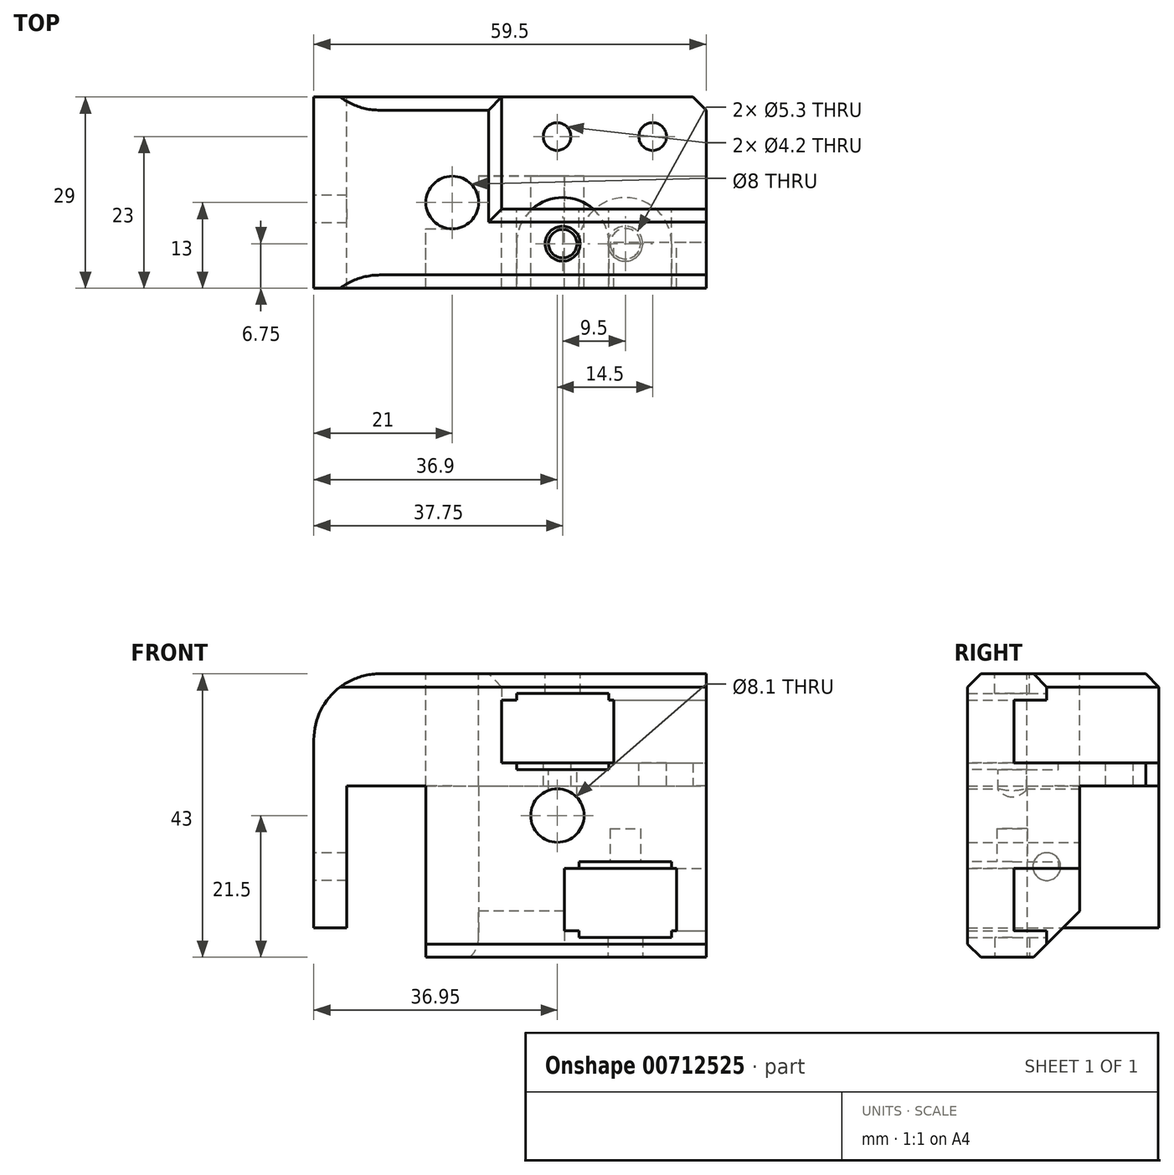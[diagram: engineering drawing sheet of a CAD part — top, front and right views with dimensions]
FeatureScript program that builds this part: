
annotation { "Feature Type Name" : "Feature", "Feature Type Description" : "" }
export const myFeature = defineFeature(function(context is Context, id is Id, definition is map)
    precondition{}
    {
        {
            var Q0;
            Q0=qCreatedBy(makeId("Front.planeOp"),FACE);
            var sketch = newSketch(context, id + "F0", { "sketchPlane" : qUnion([Q0])});
            skLineSegment(sketch, "E0", {"start": v(0, 0) * mm, "end": v(0, 28.5) * mm});
            skLineSegment(sketch, "E1", {"start": v(10, 38.5) * mm, "end": v(59.5, 38.5) * mm});
            skLineSegment(sketch, "E2", {"start": v(59.5, 38.5) * mm, "end": v(59.5, -4.5) * mm});
            skLineSegment(sketch, "E3", {"start": v(59.5, -4.5) * mm, "end": v(17, -4.5) * mm});
            skLineSegment(sketch, "E4", {"start": v(17, -4.5) * mm, "end": v(17, 21.5) * mm});
            skLineSegment(sketch, "E5", {"start": v(17, 21.5) * mm, "end": v(5, 21.5) * mm});
            skLineSegment(sketch, "E6", {"start": v(5, 21.5) * mm, "end": v(5, 0) * mm});
            skLineSegment(sketch, "E7", {"start": v(5, 0) * mm, "end": v(0, 0) * mm});
            skPoint(sketch, "E8.visualSharp", {"position": v(0, 38.5) * mm});
            skArc(sketch, "E8.filletArc", {"start": v(10, 38.5) * mm, "mid": v(2.93, 35.57) * mm, "end": v(0, 28.5) * mm});
            skCircle(sketch, "E9", {"center": v(36.95, 17) * mm, "radius": 4.05 * mm});
            skLineSegment(sketch, "E10.bottom", {"start": v(28.5, 34.5) * mm, "end": v(45.5, 34.5) * mm});
            skLineSegment(sketch, "E10.top", {"start": v(28.5, 25) * mm, "end": v(45.5, 25) * mm});
            skLineSegment(sketch, "E10.left", {"start": v(28.5, 34.5) * mm, "end": v(28.5, 25) * mm});
            skLineSegment(sketch, "E10.right", {"start": v(45.5, 34.5) * mm, "end": v(45.5, 25) * mm});
            skLineSegment(sketch, "E11.bottom", {"start": v(38, 9) * mm, "end": v(55, 9) * mm});
            skLineSegment(sketch, "E11.top", {"start": v(38, -0.5) * mm, "end": v(55, -0.5) * mm});
            skLineSegment(sketch, "E11.left", {"start": v(38, 9) * mm, "end": v(38, -0.5) * mm});
            skLineSegment(sketch, "E11.right", {"start": v(55, 9) * mm, "end": v(55, -0.5) * mm});
            skLineSegment(sketch, "E12.bottom", {"start": v(30.75, 34.5) * mm, "end": v(44.75, 34.5) * mm});
            skLineSegment(sketch, "E12.top", {"start": v(30.75, 35.5) * mm, "end": v(44.75, 35.5) * mm});
            skLineSegment(sketch, "E12.left", {"start": v(30.75, 34.5) * mm, "end": v(30.75, 35.5) * mm});
            skLineSegment(sketch, "E12.right", {"start": v(44.75, 34.5) * mm, "end": v(44.75, 35.5) * mm});
            skLineSegment(sketch, "E13.bottom", {"start": v(40.25, -0.5) * mm, "end": v(54.25, -0.5) * mm});
            skLineSegment(sketch, "E13.top", {"start": v(40.25, -1.5) * mm, "end": v(54.25, -1.5) * mm});
            skLineSegment(sketch, "E13.left", {"start": v(40.25, -0.5) * mm, "end": v(40.25, -1.5) * mm});
            skLineSegment(sketch, "E13.right", {"start": v(54.25, -0.5) * mm, "end": v(54.25, -1.5) * mm});
            skSolve(sketch);
        }
        {
            var Q0;
            Q0=makeQuery(id+"F0.imprint","IMPRINT",FACE,{"disambiguationData":[TD([[makeQuery(id+"F0.imprint","IMPRINT",EDGE,{"derivedFrom":sQuery(id+"F0.wireOp",EDGE,"E0")}),-1.0]])]});
            extrude(context, id + "F1", {"entities" : qUnion([Q0]), "depth" : 7 * mm, "offsetDistance" : 25 * mm});
        }
        {
            var Q0;
            Q0=makeQuery(id+"F1.opExtrude","CAP_EDGE",EDGE,{"disambiguationData":[OSD([sQuery(id+"F0.wireOp",EDGE,"E1")])],"isStart":false});
            var Q1;
            Q1=makeQuery(id+"F1.opExtrude","CAP_EDGE",EDGE,{"disambiguationData":[OSD([sQuery(id+"F0.wireOp",EDGE,"E3")])],"isStart":false});
            chamfer(context, id + "F2", {"entities" : qUnion([Q0, Q1]), "width" : 2 * mm});
        }
        {
            var Q0;
            Q0=makeQuery(id+"F1.opExtrude","CAP_FACE",FACE,{"disambiguationData":[OSD([sQuery(id+"F0.wireOp",EDGE,"E0"),sQuery(id+"F0.wireOp",EDGE,"E1"),sQuery(id+"F0.wireOp",EDGE,"E2"),sQuery(id+"F0.wireOp",EDGE,"E3"),sQuery(id+"F0.wireOp",EDGE,"E4"),sQuery(id+"F0.wireOp",EDGE,"E5"),sQuery(id+"F0.wireOp",EDGE,"E6"),sQuery(id+"F0.wireOp",EDGE,"E7"),sQuery(id+"F0.wireOp",EDGE,"E8.filletArc"),sQuery(id+"F0.wireOp",EDGE,"E9"),sQuery(id+"F0.wireOp",EDGE,"E10.bottom"),sQuery(id+"F0.wireOp",EDGE,"E10.top"),sQuery(id+"F0.wireOp",EDGE,"E10.left"),sQuery(id+"F0.wireOp",EDGE,"E10.right"),sQuery(id+"F0.wireOp",EDGE,"E11.bottom"),sQuery(id+"F0.wireOp",EDGE,"E11.top"),sQuery(id+"F0.wireOp",EDGE,"E11.left"),sQuery(id+"F0.wireOp",EDGE,"E11.right"),sQuery(id+"F0.wireOp",EDGE,"E12.top"),sQuery(id+"F0.wireOp",EDGE,"E12.left"),sQuery(id+"F0.wireOp",EDGE,"E12.right"),sQuery(id+"F0.wireOp",EDGE,"E13.top"),sQuery(id+"F0.wireOp",EDGE,"E13.left"),sQuery(id+"F0.wireOp",EDGE,"E13.right")])],"isStart":true});
            var sketch = newSketch(context, id + "F3", { "sketchPlane" : qUnion([Q0])});
            skLineSegment(sketch, "E14.bottom", {"start": v(-17, 21.5) * mm, "end": v(-59.5, 21.5) * mm});
            skLineSegment(sketch, "E14.top", {"start": v(-17, -4.5) * mm, "end": v(-59.5, -4.5) * mm});
            skLineSegment(sketch, "E14.left", {"start": v(-17, 21.5) * mm, "end": v(-17, -4.5) * mm});
            skLineSegment(sketch, "E14.right", {"start": v(-59.5, 21.5) * mm, "end": v(-59.5, -4.5) * mm});
            skLineSegment(sketch, "E15.bottom", {"start": v(-59.5, 38.5) * mm, "end": v(-28.5, 38.5) * mm});
            skLineSegment(sketch, "E15.top", {"start": v(-59.5, 25) * mm, "end": v(-28.5, 25) * mm});
            skLineSegment(sketch, "E15.left", {"start": v(-59.5, 38.5) * mm, "end": v(-59.5, 25) * mm});
            skLineSegment(sketch, "E15.right", {"start": v(-28.5, 38.5) * mm, "end": v(-28.5, 25) * mm});
            skSolve(sketch);
        }
        {
            var Q0;
            {var subQ0=sQuery(id+"F3.wireOp",EDGE,"E14.bottom");Q0=makeQuery(id+"F3.imprint","IMPRINT",FACE,{"disambiguationData":[TD([[makeQuery(id+"F3.imprint","IMPRINT",EDGE,{"derivedFrom":subQ0}),-1.0]])]});}
            extrude(context, id + "F4", {"entities" : qUnion([Q0]), "operationType" : NewBodyOperationType.ADD, "depth" : 22 * mm, "offsetDistance" : 25 * mm});
        }
        {
            var Q0;
            {var subQ0=sQuery(id+"F0.wireOp",EDGE,"E12.top");var subQ1=sQuery(id+"F0.wireOp",EDGE,"E10.right");var subQ2=sQuery(id+"F0.wireOp",EDGE,"E10.top");var subQ3=sQuery(id+"F0.wireOp",EDGE,"E1");var subQ4=sQuery(id+"F0.wireOp",EDGE,"E12.right");var subQ5=sQuery(id+"F0.wireOp",EDGE,"E10.bottom");var subQ7=sQuery(id+"F0.wireOp",EDGE,"E10.left");var subQ8=sQuery(id+"F0.wireOp",EDGE,"E2");var subQ9=sQuery(id+"F0.wireOp",EDGE,"E12.left");Q0=makeQuery(id+"F4.boolean.opBoolean","SPLIT",FACE,{"disambiguationData":[TD([makeQuery(id+"F1.opExtrude","SWEPT_FACE",FACE,{"disambiguationData":[OSD([subQ3])]})])],"derivedFrom":makeQuery(id+"F1.opExtrude","CAP_FACE",FACE,{"disambiguationData":[OSD([sQuery(id+"F0.wireOp",EDGE,"E0"),subQ3,subQ8,sQuery(id+"F0.wireOp",EDGE,"E3"),sQuery(id+"F0.wireOp",EDGE,"E4"),sQuery(id+"F0.wireOp",EDGE,"E5"),sQuery(id+"F0.wireOp",EDGE,"E6"),sQuery(id+"F0.wireOp",EDGE,"E7"),sQuery(id+"F0.wireOp",EDGE,"E8.filletArc"),sQuery(id+"F0.wireOp",EDGE,"E9"),subQ5,subQ2,subQ7,subQ1,sQuery(id+"F0.wireOp",EDGE,"E11.bottom"),sQuery(id+"F0.wireOp",EDGE,"E11.top"),sQuery(id+"F0.wireOp",EDGE,"E11.left"),sQuery(id+"F0.wireOp",EDGE,"E11.right"),subQ0,subQ9,subQ4,sQuery(id+"F0.wireOp",EDGE,"E13.top"),sQuery(id+"F0.wireOp",EDGE,"E13.left"),sQuery(id+"F0.wireOp",EDGE,"E13.right")])],"isStart":true})});}
            var sketch = newSketch(context, id + "F5", { "sketchPlane" : qUnion([Q0])});
            skLineSegment(sketch, "E16.bottom", {"start": v(-28.5, 34.5) * mm, "end": v(-59.5, 34.5) * mm});
            skLineSegment(sketch, "E16.top", {"start": v(-28.5, 38.5) * mm, "end": v(-59.5, 38.5) * mm});
            skLineSegment(sketch, "E16.left", {"start": v(-28.5, 34.5) * mm, "end": v(-28.5, 38.5) * mm});
            skLineSegment(sketch, "E16.right", {"start": v(-59.5, 34.5) * mm, "end": v(-59.5, 38.5) * mm});
            skSolve(sketch);
        }
        {
            var Q0;
            Q0=makeQuery(id+"F5.imprint","IMPRINT",FACE,{"disambiguationData":[TD([[makeQuery(id+"F5.imprint","IMPRINT",EDGE,{"derivedFrom":sQuery(id+"F5.wireOp",EDGE,"E16.top")}),1.0]])]});
            extrude(context, id + "F6", {"entities" : qUnion([Q0]), "operationType" : NewBodyOperationType.ADD, "depth" : 5 * mm, "offsetDistance" : 25 * mm});
        }
        {
            var Q0;
            {var subQ0=sQuery(id+"F0.wireOp",EDGE,"E11.right");var subQ1=sQuery(id+"F0.wireOp",EDGE,"E11.left");var subQ2=sQuery(id+"F0.wireOp",EDGE,"E2");var subQ3=sQuery(id+"F0.wireOp",EDGE,"E11.top");var subQ4=sQuery(id+"F0.wireOp",EDGE,"E13.right");var subQ6=sQuery(id+"F0.wireOp",EDGE,"E9");var subQ7=sQuery(id+"F0.wireOp",EDGE,"E3");var subQ8=sQuery(id+"F0.wireOp",EDGE,"E11.bottom");var subQ9=sQuery(id+"F0.wireOp",EDGE,"E4");var subQ10=sQuery(id+"F0.wireOp",EDGE,"E13.left");var subQ11=sQuery(id+"F0.wireOp",EDGE,"E5");var subQ12=sQuery(id+"F0.wireOp",EDGE,"E13.top");Q0=makeQuery(id+"F4.boolean.opBoolean","SPLIT",FACE,{"disambiguationData":[TD([makeQuery(id+"F1.opExtrude","SWEPT_FACE",FACE,{"disambiguationData":[OSD([subQ7])]})])],"derivedFrom":makeQuery(id+"F1.opExtrude","CAP_FACE",FACE,{"disambiguationData":[OSD([sQuery(id+"F0.wireOp",EDGE,"E0"),sQuery(id+"F0.wireOp",EDGE,"E1"),subQ2,subQ7,subQ9,subQ11,sQuery(id+"F0.wireOp",EDGE,"E6"),sQuery(id+"F0.wireOp",EDGE,"E7"),sQuery(id+"F0.wireOp",EDGE,"E8.filletArc"),subQ6,sQuery(id+"F0.wireOp",EDGE,"E10.bottom"),sQuery(id+"F0.wireOp",EDGE,"E10.top"),sQuery(id+"F0.wireOp",EDGE,"E10.left"),sQuery(id+"F0.wireOp",EDGE,"E10.right"),subQ8,subQ3,subQ1,subQ0,sQuery(id+"F0.wireOp",EDGE,"E12.top"),sQuery(id+"F0.wireOp",EDGE,"E12.left"),sQuery(id+"F0.wireOp",EDGE,"E12.right"),subQ12,subQ10,subQ4])],"isStart":true})});}
            var sketch = newSketch(context, id + "F7", { "sketchPlane" : qUnion([Q0])});
            skLineSegment(sketch, "E17.bottom", {"start": v(-38, -0.5) * mm, "end": v(-59.5, -0.5) * mm});
            skLineSegment(sketch, "E17.top", {"start": v(-38, 9) * mm, "end": v(-59.5, 9) * mm});
            skLineSegment(sketch, "E17.left", {"start": v(-38, -0.5) * mm, "end": v(-38, 9) * mm});
            skLineSegment(sketch, "E17.right", {"start": v(-59.5, -0.5) * mm, "end": v(-59.5, 9) * mm});
            skSolve(sketch);
        }
        {
            var Q0;
            {var subQ5=sQuery(id+"F7.wireOp",EDGE,"E17.left");Q0=makeQuery(id+"F7.imprint","IMPRINT",FACE,{"disambiguationData":[TD([[makeQuery(id+"F7.imprint","IMPRINT",EDGE,{"derivedFrom":subQ5}),1.0]])]});}
            extrude(context, id + "F8", {"entities" : qUnion([Q0]), "operationType" : NewBodyOperationType.ADD, "depth" : 2 * mm, "offsetDistance" : 25 * mm});
        }
        {
            var Q0;
            Q0=makeQuery(id+"F8.opExtrude","CAP_FACE",FACE,{"disambiguationData":[OSD([sQuery(id+"F0.wireOp",EDGE,"E2"),sQuery(id+"F0.wireOp",EDGE,"E3"),sQuery(id+"F0.wireOp",EDGE,"E4"),sQuery(id+"F0.wireOp",EDGE,"E5"),sQuery(id+"F0.wireOp",EDGE,"E9"),sQuery(id+"F0.wireOp",EDGE,"E13.top"),sQuery(id+"F0.wireOp",EDGE,"E13.left"),sQuery(id+"F0.wireOp",EDGE,"E13.right"),sQuery(id+"F3.wireOp",EDGE,"E14.bottom"),sQuery(id+"F7.wireOp",EDGE,"E17.bottom"),sQuery(id+"F7.wireOp",EDGE,"E17.top"),sQuery(id+"F7.wireOp",EDGE,"E17.left")])],"isStart":false});
            var sketch = newSketch(context, id + "F9", { "sketchPlane" : qUnion([Q0])});
            skLineSegment(sketch, "E18.bottom", {"start": v(-17, 21.5) * mm, "end": v(-21, 21.5) * mm});
            skLineSegment(sketch, "E18.top", {"start": v(-17, -4.5) * mm, "end": v(-21, -4.5) * mm});
            skLineSegment(sketch, "E18.left", {"start": v(-17, 21.5) * mm, "end": v(-17, -4.5) * mm});
            skLineSegment(sketch, "E18.right", {"start": v(-21, 21.5) * mm, "end": v(-21, -4.5) * mm});
            skSolve(sketch);
        }
        {
            var Q0;
            {var subQ15=sQuery(id+"F9.wireOp",EDGE,"E18.right");Q0=makeQuery(id+"F9.imprint","IMPRINT",FACE,{"disambiguationData":[TD([[makeQuery(id+"F9.imprint","IMPRINT",EDGE,{"derivedFrom":subQ15}),-1.0]])]});}
            extrude(context, id + "F10", {"entities" : qUnion([Q0]), "operationType" : NewBodyOperationType.ADD, "depth" : 3 * mm, "offsetDistance" : 25 * mm});
        }
        {
            var Q0;
            Q0=makeQuery(id+"F10.opExtrude","CAP_FACE",FACE,{"disambiguationData":[OSD([sQuery(id+"F0.wireOp",EDGE,"E2"),sQuery(id+"F0.wireOp",EDGE,"E3"),sQuery(id+"F0.wireOp",EDGE,"E5"),sQuery(id+"F0.wireOp",EDGE,"E9"),sQuery(id+"F0.wireOp",EDGE,"E13.top"),sQuery(id+"F0.wireOp",EDGE,"E13.left"),sQuery(id+"F0.wireOp",EDGE,"E13.right"),sQuery(id+"F3.wireOp",EDGE,"E14.bottom"),sQuery(id+"F7.wireOp",EDGE,"E17.bottom"),sQuery(id+"F7.wireOp",EDGE,"E17.top"),sQuery(id+"F7.wireOp",EDGE,"E17.left"),sQuery(id+"F9.wireOp",EDGE,"E18.right")])],"isStart":false});
            var sketch = newSketch(context, id + "F11", { "sketchPlane" : qUnion([Q0])});
            skLineSegment(sketch, "E19.bottom", {"start": v(-38, -0.5) * mm, "end": v(-59.5, -0.5) * mm});
            skLineSegment(sketch, "E19.top", {"start": v(-38, -4.5) * mm, "end": v(-59.5, -4.5) * mm});
            skLineSegment(sketch, "E19.left", {"start": v(-38, -0.5) * mm, "end": v(-38, -4.5) * mm});
            skLineSegment(sketch, "E19.right", {"start": v(-59.5, -0.5) * mm, "end": v(-59.5, -4.5) * mm});
            skSolve(sketch);
        }
        {
            var Q0;
            {var subQ2=sQuery(id+"F11.wireOp",EDGE,"E19.left");Q0=makeQuery(id+"F11.imprint","IMPRINT",FACE,{"disambiguationData":[TD([[makeQuery(id+"F11.imprint","IMPRINT",EDGE,{"derivedFrom":subQ2}),1.0]])]});}
            extrude(context, id + "F12", {"entities" : qUnion([Q0]), "operationType" : NewBodyOperationType.ADD, "depth" : 5 * mm, "offsetDistance" : 25 * mm});
        }
        {
            var Q0;
            Q0=makeQuery(id+"F12.opExtrude","CAP_EDGE",EDGE,{"disambiguationData":[OSD([sQuery(id+"F0.wireOp",EDGE,"E3")])],"isStart":false});
            chamfer(context, id + "F13", {"entities" : qUnion([Q0]), "width" : 7 * mm, "tangentPropagation" : true});
        }
        {
            var Q0;
            Q0=makeQuery(id+"F6.opExtrude","CAP_EDGE",EDGE,{"disambiguationData":[OSD([sQuery(id+"F5.wireOp",EDGE,"E16.top")])],"isStart":false});
            var Q1;
            Q1=makeQuery(id+"F4.opExtrude","CAP_EDGE",EDGE,{"disambiguationData":[OSD([sQuery(id+"F0.wireOp",EDGE,"E2")])],"isStart":false});
            chamfer(context, id + "F14", {"entities" : qUnion([Q0, Q1]), "width" : 2 * mm, "tangentPropagation" : true});
        }
        {
            var Q0;
            Q0=qCreatedBy(makeId("Top.planeOp"),FACE);
            var sketch = newSketch(context, id + "F15", { "sketchPlane" : qUnion([Q0])});
            skCircle(sketch, "E20", {"center": v(21, 6) * mm, "radius": 4 * mm});
            skSolve(sketch);
        }
        {
            var Q0;
            {var subQ0=sQuery(id+"F9.wireOp",EDGE,"E18.right");Q0=makeQuery(id+"F12.boolean.opBoolean","MERGE",FACE,{"derivedFrom":[makeQuery(id+"F10.opExtrude","SWEPT_FACE",FACE,{"disambiguationData":[OSD([subQ0])]}),makeQuery(id+"F12.opExtrude","SWEPT_FACE",FACE,{"disambiguationData":[OSD([subQ0])]})]});}
            var sketch = newSketch(context, id + "F16", { "sketchPlane" : qUnion([Q0])});
            skLineSegment(sketch, "E21.bottom", {"start": v(-10, 21.5) * mm, "end": v(-6, 21.5) * mm});
            skLineSegment(sketch, "E21.top", {"start": v(-10, -13.36) * mm, "end": v(-6, -13.36) * mm});
            skLineSegment(sketch, "E21.left", {"start": v(-10, 21.5) * mm, "end": v(-10, -13.36) * mm});
            skLineSegment(sketch, "E21.right", {"start": v(-6, 21.5) * mm, "end": v(-6, -13.36) * mm});
            skSolve(sketch);
        }
        {
            var Q0;
            {var subQ0=sQuery(id+"F16.wireOp",EDGE,"E21.bottom");Q0=makeQuery(id+"F16.imprint","IMPRINT",FACE,{"disambiguationData":[TD([[makeQuery(id+"F16.imprint","IMPRINT",EDGE,{"derivedFrom":subQ0}),-1.0]])]});}
            extrude(context, id + "F17", {"entities" : qUnion([Q0]), "operationType" : NewBodyOperationType.REMOVE, "oppositeDirection" : true, "depth" : 4 * mm, "offsetDistance" : 25 * mm});
        }
        {
            var Q0;
            Q0=makeQuery(id+"F15.imprint","IMPRINT",FACE,{"disambiguationData":[TD([[makeQuery(id+"F15.imprint","IMPRINT",EDGE,{"derivedFrom":sQuery(id+"F15.wireOp",EDGE,"E20")}),1.0]])]});
            extrude(context, id + "F18", {"entities" : qUnion([Q0]), "operationType" : NewBodyOperationType.REMOVE, "endBound" : BoundingType.THROUGH_ALL, "oppositeDirection" : true, "depth" : 25 * mm, "offsetDistance" : 25 * mm, "hasSecondDirection" : true, "secondDirectionBound" : BoundingType.THROUGH_ALL, "secondDirectionOppositeDirection" : false, "secondDirectionDepth" : 25 * mm});
        }
        {
            var Q0;
            {var subQ0=sQuery(id+"F0.wireOp",EDGE,"E3");Q0=makeQuery(id+"F12.boolean.opBoolean","MERGE",FACE,{"derivedFrom":[makeQuery(id+"F10.boolean.opBoolean","MERGE",FACE,{"derivedFrom":[makeQuery(id+"F8.boolean.opBoolean","MERGE",FACE,{"derivedFrom":[makeQuery(id+"F1.opExtrude","SWEPT_FACE",FACE,{"disambiguationData":[OSD([subQ0])]}),makeQuery(id+"F8.opExtrude","SWEPT_FACE",FACE,{"disambiguationData":[OSD([subQ0])]})]}),makeQuery(id+"F10.opExtrude","SWEPT_FACE",FACE,{"disambiguationData":[OSD([subQ0])]})]}),makeQuery(id+"F12.opExtrude","SWEPT_FACE",FACE,{"disambiguationData":[OSD([subQ0])]})]});}
            var sketch = newSketch(context, id + "F19", { "sketchPlane" : qUnion([Q0])});
            skCircle(sketch, "E22", {"center": v(47.25, 0.25) * mm, "radius": 2.3 * mm});
            skSolve(sketch);
        }
        {
            var Q0;
            Q0=makeQuery(id+"F19.imprint","IMPRINT",FACE,{"disambiguationData":[TD([[makeQuery(id+"F19.imprint","IMPRINT",EDGE,{"derivedFrom":sQuery(id+"F19.wireOp",EDGE,"E22")}),1.0]])]});
            extrude(context, id + "F20", {"entities" : qUnion([Q0]), "operationType" : NewBodyOperationType.REMOVE, "oppositeDirection" : true, "depth" : 19.5 * mm, "offsetDistance" : 25 * mm});
        }
        {
            var Q0;
            {var subQ0=sQuery(id+"F0.wireOp",EDGE,"E3");Q0=makeQuery(id+"F12.boolean.opBoolean","MERGE",FACE,{"derivedFrom":[makeQuery(id+"F10.boolean.opBoolean","MERGE",FACE,{"derivedFrom":[makeQuery(id+"F8.boolean.opBoolean","MERGE",FACE,{"derivedFrom":[makeQuery(id+"F1.opExtrude","SWEPT_FACE",FACE,{"disambiguationData":[OSD([subQ0])]}),makeQuery(id+"F8.opExtrude","SWEPT_FACE",FACE,{"disambiguationData":[OSD([subQ0])]})]}),makeQuery(id+"F10.opExtrude","SWEPT_FACE",FACE,{"disambiguationData":[OSD([subQ0])]})]}),makeQuery(id+"F12.opExtrude","SWEPT_FACE",FACE,{"disambiguationData":[OSD([subQ0])]})]});}
            var sketch = newSketch(context, id + "F21", { "sketchPlane" : qUnion([Q0])});
            skCircle(sketch, "E23", {"center": v(47.25, 0.25) * mm, "radius": 2.65 * mm});
            skSolve(sketch);
        }
        {
            var Q0;
            Q0=makeQuery(id+"F21.imprint","IMPRINT",FACE,{"disambiguationData":[TD([[makeQuery(id+"F21.imprint","IMPRINT",EDGE,{"derivedFrom":sQuery(id+"F21.wireOp",EDGE,"E23")}),1.0]])]});
            extrude(context, id + "F22", {"entities" : qUnion([Q0]), "operationType" : NewBodyOperationType.REMOVE, "endBound" : BoundingType.UP_TO_NEXT, "oppositeDirection" : true, "depth" : 25 * mm, "offsetDistance" : 25 * mm});
        }
        {
            var Q0;
            {var subQ0=sQuery(id+"F0.wireOp",EDGE,"E1");Q0=makeQuery(id+"F6.boolean.opBoolean","MERGE",FACE,{"derivedFrom":[makeQuery(id+"F4.boolean.opBoolean","MERGE",FACE,{"derivedFrom":[makeQuery(id+"F1.opExtrude","SWEPT_FACE",FACE,{"disambiguationData":[OSD([subQ0])]}),makeQuery(id+"F4.opExtrude","SWEPT_FACE",FACE,{"disambiguationData":[OSD([subQ0])]})]}),makeQuery(id+"F6.opExtrude","SWEPT_FACE",FACE,{"disambiguationData":[OSD([sQuery(id+"F5.wireOp",EDGE,"E16.top")])]})]});}
            var sketch = newSketch(context, id + "F23", { "sketchPlane" : qUnion([Q0])});
            skCircle(sketch, "E24", {"center": v(37.75, -0.25) * mm, "radius": 2.15 * mm});
            skSolve(sketch);
        }
        {
            var Q0;
            Q0=makeQuery(id+"F23.imprint","IMPRINT",FACE,{"disambiguationData":[TD([[makeQuery(id+"F23.imprint","IMPRINT",EDGE,{"derivedFrom":sQuery(id+"F23.wireOp",EDGE,"E24")}),1.0]])]});
            extrude(context, id + "F24", {"entities" : qUnion([Q0]), "operationType" : NewBodyOperationType.REMOVE, "oppositeDirection" : true, "depth" : 22 * mm, "offsetDistance" : 25 * mm});
        }
        {
            var Q0;
            {var subQ0=sQuery(id+"F0.wireOp",EDGE,"E1");Q0=makeQuery(id+"F6.boolean.opBoolean","MERGE",FACE,{"derivedFrom":[makeQuery(id+"F4.boolean.opBoolean","MERGE",FACE,{"derivedFrom":[makeQuery(id+"F1.opExtrude","SWEPT_FACE",FACE,{"disambiguationData":[OSD([subQ0])]}),makeQuery(id+"F4.opExtrude","SWEPT_FACE",FACE,{"disambiguationData":[OSD([subQ0])]})]}),makeQuery(id+"F6.opExtrude","SWEPT_FACE",FACE,{"disambiguationData":[OSD([sQuery(id+"F5.wireOp",EDGE,"E16.top")])]})]});}
            var sketch = newSketch(context, id + "F25", { "sketchPlane" : qUnion([Q0])});
            skCircle(sketch, "E25", {"center": v(37.75, -0.25) * mm, "radius": 2.65 * mm});
            skSolve(sketch);
        }
        {
            var Q0;
            Q0=makeQuery(id+"F25.imprint","IMPRINT",FACE,{"disambiguationData":[TD([[makeQuery(id+"F25.imprint","IMPRINT",EDGE,{"derivedFrom":sQuery(id+"F25.wireOp",EDGE,"E25")}),1.0]])]});
            extrude(context, id + "F26", {"entities" : qUnion([Q0]), "operationType" : NewBodyOperationType.REMOVE, "endBound" : BoundingType.UP_TO_NEXT, "oppositeDirection" : true, "depth" : 25 * mm, "offsetDistance" : 25 * mm});
        }
        {
            var Q0;
            Q0=makeQuery(id+"F4.boolean.opBoolean","MERGE",FACE,{"derivedFrom":[makeQuery(id+"F1.opExtrude","SWEPT_FACE",FACE,{"disambiguationData":[OSD([sQuery(id+"F0.wireOp",EDGE,"E10.top")])]}),makeQuery(id+"F4.opExtrude","SWEPT_FACE",FACE,{"disambiguationData":[OSD([sQuery(id+"F3.wireOp",EDGE,"E15.top")])]})]});
            var sketch = newSketch(context, id + "F27", { "sketchPlane" : qUnion([Q0])});
            skCircle(sketch, "E26", {"center": v(37.75, -0.25) * mm, "radius": 7 * mm});
            skLineSegment(sketch, "E27.bottom", {"start": v(30.75, -0.25) * mm, "end": v(44.75, -0.25) * mm});
            skLineSegment(sketch, "E27.top", {"start": v(30.75, -7) * mm, "end": v(44.75, -7) * mm});
            skLineSegment(sketch, "E27.left", {"start": v(30.75, -0.25) * mm, "end": v(30.75, -7) * mm});
            skLineSegment(sketch, "E27.right", {"start": v(44.75, -0.25) * mm, "end": v(44.75, -7) * mm});
            skSolve(sketch);
        }
        {
            var Q0;
            {var subQ0=sQuery(id+"F27.wireOp",EDGE,"E27.left");Q0=makeQuery(id+"F27.imprint","IMPRINT",FACE,{"disambiguationData":[TD([[makeQuery(id+"F27.imprint","IMPRINT",EDGE,{"derivedFrom":subQ0}),1.0]])]});}
            var Q1;
            {var subQ1=sQuery(id+"F27.wireOp",EDGE,"E26");var subQ6=sQuery(id+"F27.wireOp",EDGE,"E27.top");var subQ9=makeQuery(id+"F27.imprint","INTERSECT",VERTEX,{"disambiguationData":[OD(0.0)],"derivedFrom":[subQ1,subQ6]});Q1=makeQuery(id+"F27.imprint","IMPRINT",FACE,{"disambiguationData":[TD([[makeQuery(id+"F27.imprint","IMPRINT",EDGE,{"disambiguationData":[TD([[subQ9,-1.0]])],"derivedFrom":subQ6}),1.0]])]});}
            var Q2;
            {var subQ0=sQuery(id+"F27.wireOp",EDGE,"E27.bottom");var subQ1=sQuery(id+"F27.wireOp",EDGE,"E26");var subQ2=makeQuery(id+"F27.imprint","INTERSECT",VERTEX,{"derivedFrom":[subQ1,subQ0,sQuery(id+"F27.wireOp",EDGE,"E27.left")]});Q2=makeQuery(id+"F27.imprint","IMPRINT",FACE,{"disambiguationData":[TD([[makeQuery(id+"F27.imprint","IMPRINT",EDGE,{"disambiguationData":[TD([[subQ2,1.0]])],"derivedFrom":subQ1}),1.0]])]});}
            var Q3;
            {var subQ0=sQuery(id+"F27.wireOp",EDGE,"E27.right");Q3=makeQuery(id+"F27.imprint","IMPRINT",FACE,{"disambiguationData":[TD([[makeQuery(id+"F27.imprint","IMPRINT",EDGE,{"derivedFrom":subQ0}),-1.0]])]});}
            extrude(context, id + "F28", {"entities" : qUnion([Q0, Q1, Q2, Q3]), "operationType" : NewBodyOperationType.REMOVE, "oppositeDirection" : true, "depth" : 1 * mm, "offsetDistance" : 25 * mm});
        }
        {
            var Q0;
            {var subQ0=sQuery(id+"F7.wireOp",EDGE,"E17.top");Q0=makeQuery(id+"F12.boolean.opBoolean","MERGE",FACE,{"derivedFrom":[makeQuery(id+"F10.boolean.opBoolean","MERGE",FACE,{"derivedFrom":[makeQuery(id+"F8.boolean.opBoolean","MERGE",FACE,{"derivedFrom":[makeQuery(id+"F1.opExtrude","SWEPT_FACE",FACE,{"disambiguationData":[OSD([sQuery(id+"F0.wireOp",EDGE,"E11.bottom")])]}),makeQuery(id+"F8.opExtrude","SWEPT_FACE",FACE,{"disambiguationData":[OSD([subQ0])]})]}),makeQuery(id+"F10.opExtrude","SWEPT_FACE",FACE,{"disambiguationData":[OSD([subQ0])]})]}),makeQuery(id+"F12.opExtrude","SWEPT_FACE",FACE,{"disambiguationData":[OSD([subQ0])]})]});}
            var sketch = newSketch(context, id + "F29", { "sketchPlane" : qUnion([Q0])});
            skCircle(sketch, "E28", {"center": v(47.25, 0.25) * mm, "radius": 7 * mm});
            skLineSegment(sketch, "E29.bottom", {"start": v(40.25, 0.25) * mm, "end": v(54.25, 0.25) * mm});
            skLineSegment(sketch, "E29.top", {"start": v(40.25, 7) * mm, "end": v(54.25, 7) * mm});
            skLineSegment(sketch, "E29.left", {"start": v(40.25, 0.25) * mm, "end": v(40.25, 7) * mm});
            skLineSegment(sketch, "E29.right", {"start": v(54.25, 0.25) * mm, "end": v(54.25, 7) * mm});
            skSolve(sketch);
        }
        {
            var Q0;
            {var subQ0=sQuery(id+"F29.wireOp",EDGE,"E29.bottom");var subQ1=sQuery(id+"F29.wireOp",EDGE,"E28");var subQ2=makeQuery(id+"F29.imprint","INTERSECT",VERTEX,{"derivedFrom":[subQ1,subQ0,sQuery(id+"F29.wireOp",EDGE,"E29.left")]});Q0=makeQuery(id+"F29.imprint","IMPRINT",FACE,{"disambiguationData":[TD([[makeQuery(id+"F29.imprint","IMPRINT",EDGE,{"disambiguationData":[TD([[subQ2,-1.0]])],"derivedFrom":subQ1}),1.0]])]});}
            var Q1;
            {var subQ1=sQuery(id+"F29.wireOp",EDGE,"E28");var subQ8=sQuery(id+"F29.wireOp",EDGE,"E29.top");var subQ10=makeQuery(id+"F29.imprint","INTERSECT",VERTEX,{"disambiguationData":[OD(0.0)],"derivedFrom":[subQ1,subQ8]});Q1=makeQuery(id+"F29.imprint","IMPRINT",FACE,{"disambiguationData":[TD([[makeQuery(id+"F29.imprint","IMPRINT",EDGE,{"disambiguationData":[TD([[subQ10,1.0]])],"derivedFrom":subQ8}),-1.0]])]});}
            var Q2;
            {var subQ0=sQuery(id+"F29.wireOp",EDGE,"E29.left");Q2=makeQuery(id+"F29.imprint","IMPRINT",FACE,{"disambiguationData":[TD([[makeQuery(id+"F29.imprint","IMPRINT",EDGE,{"derivedFrom":subQ0}),-1.0]])]});}
            var Q3;
            {var subQ0=sQuery(id+"F29.wireOp",EDGE,"E29.right");Q3=makeQuery(id+"F29.imprint","IMPRINT",FACE,{"disambiguationData":[TD([[makeQuery(id+"F29.imprint","IMPRINT",EDGE,{"derivedFrom":subQ0}),1.0]])]});}
            extrude(context, id + "F30", {"entities" : qUnion([Q0, Q1, Q2, Q3]), "operationType" : NewBodyOperationType.REMOVE, "oppositeDirection" : true, "depth" : 1 * mm, "offsetDistance" : 25 * mm});
        }
        {
            var Q0;
            Q0=makeQuery(id+"F4.boolean.opBoolean","MERGE",FACE,{"derivedFrom":[makeQuery(id+"F1.opExtrude","SWEPT_FACE",FACE,{"disambiguationData":[OSD([sQuery(id+"F0.wireOp",EDGE,"E10.top")])]}),makeQuery(id+"F4.opExtrude","SWEPT_FACE",FACE,{"disambiguationData":[OSD([sQuery(id+"F3.wireOp",EDGE,"E15.top")])]})]});
            var sketch = newSketch(context, id + "F31", { "sketchPlane" : qUnion([Q0])});
            skCircle(sketch, "E30", {"center": v(36.9, 16) * mm, "radius": 2.1 * mm});
            skCircle(sketch, "E31", {"center": v(51.4, 16) * mm, "radius": 2.1 * mm});
            skSolve(sketch);
        }
        {
            var Q0;
            Q0=makeQuery(id+"F31.imprint","IMPRINT",FACE,{"disambiguationData":[TD([[makeQuery(id+"F31.imprint","IMPRINT",EDGE,{"derivedFrom":sQuery(id+"F31.wireOp",EDGE,"E30")}),1.0]])]});
            var Q1;
            Q1=makeQuery(id+"F31.imprint","IMPRINT",FACE,{"disambiguationData":[TD([[makeQuery(id+"F31.imprint","IMPRINT",EDGE,{"derivedFrom":sQuery(id+"F31.wireOp",EDGE,"E31")}),1.0]])]});
            extrude(context, id + "F32", {"entities" : qUnion([Q0, Q1]), "operationType" : NewBodyOperationType.REMOVE, "endBound" : BoundingType.THROUGH_ALL, "oppositeDirection" : true, "depth" : 25 * mm, "offsetDistance" : 25 * mm});
        }
        {
            var Q0;
            Q0=makeQuery(id+"F4.opExtrude","CAP_EDGE",EDGE,{"disambiguationData":[OSD([sQuery(id+"F0.wireOp",EDGE,"E1")])],"isStart":false});
            var Q1;
            Q1=makeQuery(id+"F4.opExtrude","SWEPT_EDGE",EDGE,{"disambiguationData":[OSD([sQuery(id+"F0.wireOp",EDGE,"E1"),sQuery(id+"F3.wireOp",EDGE,"E15.bottom"),sQuery(id+"F3.wireOp",EDGE,"E15.right")])]});
            chamfer(context, id + "F33", {"entities" : qUnion([Q0, Q1]), "width" : 2 * mm});
        }
        {
            var Q0;
            {var subQ0=sQuery(id+"F0.wireOp",EDGE,"E0");Q0=makeQuery(id+"F4.boolean.opBoolean","MERGE",FACE,{"derivedFrom":[makeQuery(id+"F1.opExtrude","SWEPT_FACE",FACE,{"disambiguationData":[OSD([subQ0])]}),makeQuery(id+"F4.opExtrude","SWEPT_FACE",FACE,{"disambiguationData":[OSD([subQ0])]})]});}
            var sketch = newSketch(context, id + "F34", { "sketchPlane" : qUnion([Q0])});
            skCircle(sketch, "E32", {"center": v(-5, 9.25) * mm, "radius": 2.1 * mm});
            skSolve(sketch);
        }
        {
            var Q0;
            Q0=makeQuery(id+"F34.imprint","IMPRINT",FACE,{"disambiguationData":[TD([[makeQuery(id+"F34.imprint","IMPRINT",EDGE,{"derivedFrom":sQuery(id+"F34.wireOp",EDGE,"E32")}),1.0]])]});
            extrude(context, id + "F35", {"entities" : qUnion([Q0]), "operationType" : NewBodyOperationType.REMOVE, "endBound" : BoundingType.UP_TO_NEXT, "oppositeDirection" : true, "depth" : 25 * mm, "offsetDistance" : 25 * mm});
        }
    });
